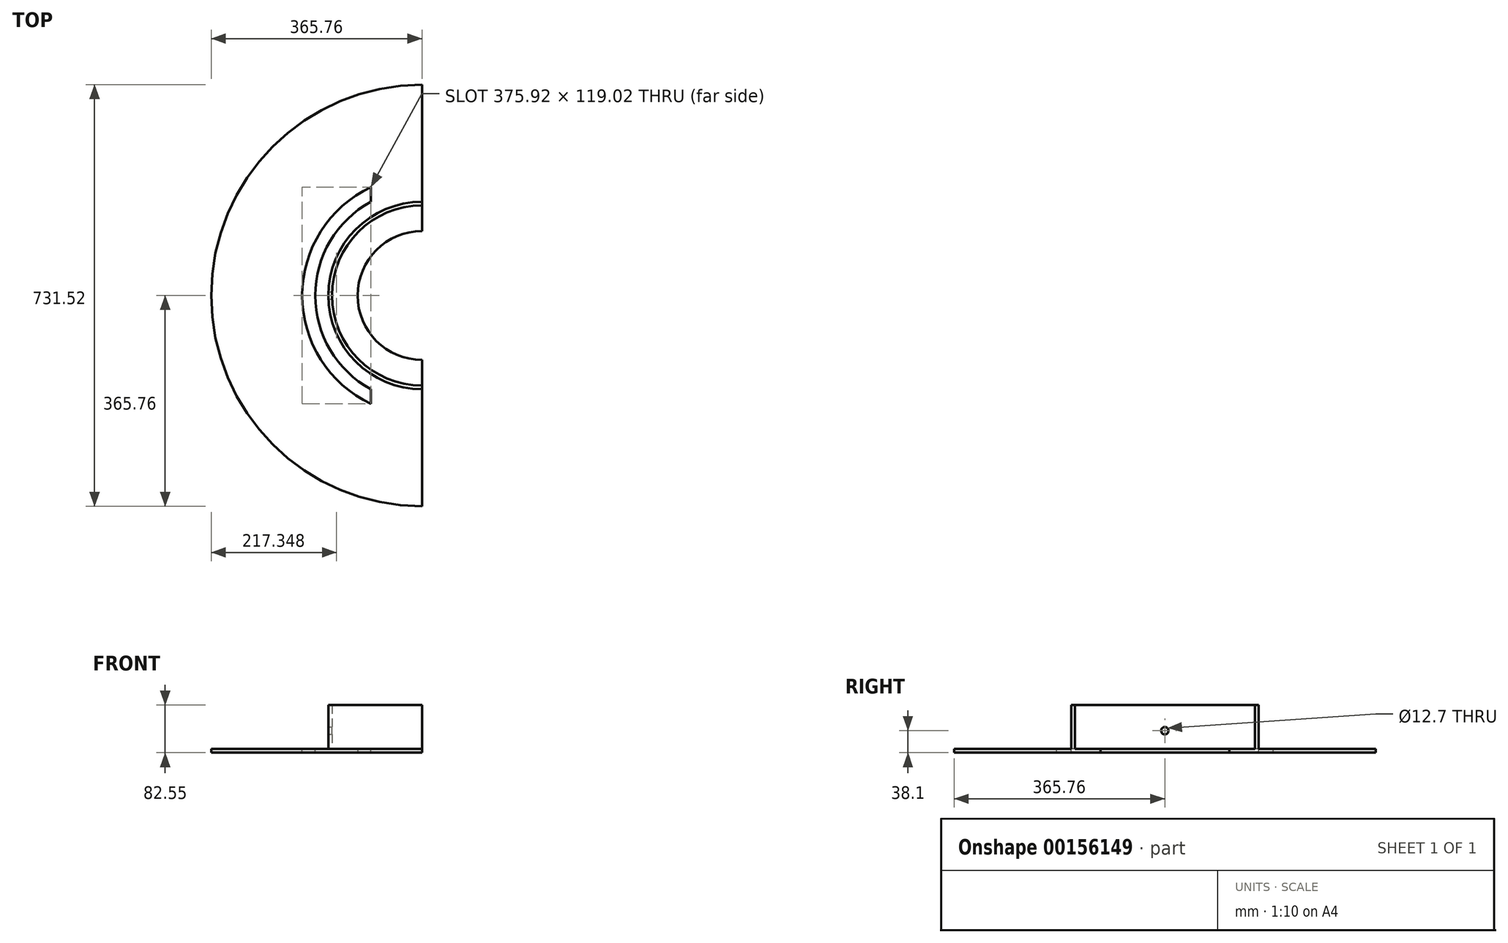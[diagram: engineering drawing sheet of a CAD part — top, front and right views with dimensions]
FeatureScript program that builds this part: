
annotation { "Feature Type Name" : "Feature", "Feature Type Description" : "" }
export const myFeature = defineFeature(function(context is Context, id is Id, definition is map)
    precondition{}
    {
        {
            var Q0;
            Q0=qCreatedBy(makeId("Top.planeOp"),FACE);
            var sketch = newSketch(context, id + "F0", { "sketchPlane" : qUnion([Q0])});
            skCircle(sketch, "E0", {"center": v(0, 0) * mm, "radius": 111.76 * mm});
            skCircle(sketch, "E1", {"center": v(0, 0) * mm, "radius": 365.76 * mm});
            skSolve(sketch);
        }
        {
            var Q0;
            Q0=makeQuery(id+"F0.imprint","IMPRINT",FACE,{"disambiguationData":[TD([[makeQuery(id+"F0.imprint","IMPRINT",EDGE,{"derivedFrom":sQuery(id+"F0.wireOp",EDGE,"E0")}),-1.0]])]});
            extrude(context, id + "F1", {"entities" : qUnion([Q0]), "depth" : 6.35 * mm});
        }
        {
            var Q0;
            Q0=makeQuery(id+"F1.opExtrude","CAP_FACE",FACE,{"disambiguationData":[OSD([sQuery(id+"F0.wireOp",EDGE,"E0"),sQuery(id+"F0.wireOp",EDGE,"E1")])],"isStart":false});
            var sketch = newSketch(context, id + "F2", { "sketchPlane" : qUnion([Q0])});
            skLineSegment(sketch, "E2.bottom", {"start": v(0, 394.93) * mm, "end": v(380.01, 394.93) * mm});
            skLineSegment(sketch, "E2.top", {"start": v(0, -392.69) * mm, "end": v(380.01, -392.69) * mm});
            skLineSegment(sketch, "E2.left", {"start": v(0, 394.93) * mm, "end": v(0, -392.69) * mm});
            skLineSegment(sketch, "E2.right", {"start": v(380.01, 394.93) * mm, "end": v(380.01, -392.69) * mm});
            skSolve(sketch);
        }
        {
            var Q0;
            Q0=qSketchRegion(id+"F2",true);
            extrude(context, id + "F3", {"entities" : qUnion([Q0]), "operationType" : NewBodyOperationType.REMOVE, "endBound" : BoundingType.THROUGH_ALL, "oppositeDirection" : true, "depth" : 25.4 * mm});
        }
        {
            var Q0;
            Q0=makeQuery(id+"F1.opExtrude","CAP_FACE",FACE,{"disambiguationData":[OSD([sQuery(id+"F0.wireOp",EDGE,"E0"),sQuery(id+"F0.wireOp",EDGE,"E1")])],"isStart":false});
            var sketch = newSketch(context, id + "F4", { "sketchPlane" : qUnion([Q0])});
            skLineSegment(sketch, "E3.right", {"start": v(-88.9, -289.56) * mm, "end": v(-88.9, -264.16) * mm});
            skLineSegment(sketch, "E4.right", {"start": v(-88.9, 264.16) * mm, "end": v(-88.9, 289.56) * mm});
            skPoint(sketch, "E5.middle.positionSnap0", {"position": v(-365.76, 0) * mm});
            skPoint(sketch, "E5.centerSnap0", {"position": v(-365.76, 0) * mm});
            skLineSegment(sketch, "E6.left", {"start": v(-88.9, -162.56) * mm, "end": v(-88.9, -187.96) * mm});
            skLineSegment(sketch, "E7.left", {"start": v(-88.9, 187.96) * mm, "end": v(-88.9, 162.56) * mm});
            skCircle(sketch, "E8", {"center": v(0, 0) * mm, "radius": 302.9 * mm});
            skCircle(sketch, "E9", {"center": v(0, 0) * mm, "radius": 278.72 * mm});
            skCircle(sketch, "E10", {"center": v(0, 0) * mm, "radius": 207.92 * mm});
            skCircle(sketch, "E11", {"center": v(0, 0) * mm, "radius": 185.28 * mm});
            skLineSegment(sketch, "E12", {"start": v(-88.9, 289.56) * mm, "end": v(-88.9, 264.16) * mm});
            skLineSegment(sketch, "E13", {"start": v(-88.9, -264.16) * mm, "end": v(-88.9, -289.56) * mm});
            skSolve(sketch);
        }
        {
            var Q0;
            {var subQ0=sQuery(id+"F4.wireOp",EDGE,"E12");Q0=makeQuery(id+"F4.imprint","IMPRINT",FACE,{"disambiguationData":[TD([[makeQuery(id+"F4.imprint","IMPRINT",EDGE,{"derivedFrom":subQ0}),-1.0]])]});}
            var Q1;
            {var subQ0=sQuery(id+"F4.wireOp",EDGE,"E7.left");Q1=makeQuery(id+"F4.imprint","IMPRINT",FACE,{"disambiguationData":[TD([[makeQuery(id+"F4.imprint","IMPRINT",EDGE,{"derivedFrom":subQ0}),-1.0]])]});}
            extrude(context, id + "F5", {"entities" : qUnion([Q0, Q1]), "operationType" : NewBodyOperationType.REMOVE, "endBound" : BoundingType.THROUGH_ALL, "oppositeDirection" : true, "depth" : 25.4 * mm});
        }
        {
            var Q0;
            Q0=makeQuery(id+"F1.opExtrude","CAP_FACE",FACE,{"disambiguationData":[OSD([sQuery(id+"F0.wireOp",EDGE,"E0"),sQuery(id+"F0.wireOp",EDGE,"E1")])],"isStart":false});
            var sketch = newSketch(context, id + "F6", { "sketchPlane" : qUnion([Q0])});
            skArc(sketch, "E14.0", {"start": v(0, 162.56) * mm, "mid": v(-162.56, 0) * mm, "end": v(0, -162.56) * mm});
            skArc(sketch, "E15.0", {"start": v(0, 156.21) * mm, "mid": v(-156.21, 0) * mm, "end": v(0, -156.21) * mm});
            skLineSegment(sketch, "E16", {"start": v(0, 162.56) * mm, "end": v(0, 156.21) * mm});
            skLineSegment(sketch, "E17", {"start": v(0, -156.21) * mm, "end": v(0, -162.56) * mm});
            skSolve(sketch);
        }
        {
            var Q0;
            Q0 = qSketchRegion(id + "F6", true);
            extrude(context, id + "F7", {"entities" : qUnion([Q0]), "operationType" : NewBodyOperationType.ADD, "depth" : 76.2 * mm, "offsetDistance" : 25.4 * mm});
        }
        {
            var Q0;
            Q0=qCreatedBy(makeId("Right.planeOp"),FACE);
            var sketch = newSketch(context, id + "F8", { "sketchPlane" : qUnion([Q0])});
            skCircle(sketch, "E18", {"center": v(0, 38.1) * mm, "radius": 6.35 * mm});
            skSolve(sketch);
        }
        {
            var Q0;
            Q0 = qSketchRegion(id + "F8", true);
            extrude(context, id + "F9", {"entities" : qUnion([Q0]), "operationType" : NewBodyOperationType.REMOVE, "endBound" : BoundingType.THROUGH_ALL, "oppositeDirection" : true, "depth" : 25.4 * mm, "offsetDistance" : 25.4 * mm});
        }
    });
